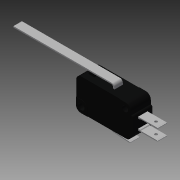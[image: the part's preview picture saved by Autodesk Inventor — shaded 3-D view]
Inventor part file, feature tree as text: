
AUTODESK INVENTOR PART (.ipt)
format: ipt  version: 2018 (Build 220112000, 112)  size: 339,968 bytes
history: native  units: in
note: dims shown in document units (in); Inventor stores cm internally (conversion verified against a paired STEP export)
features: extrude x6, sketch x2, hole x2
ambient origin geometry x8: Origin, YZ Plane, XZ Plane, XY Plane, X Axis, Y Axis, Z Axis, Center Point
bodies: Solid1 (feature_tree)
feature tree (10):
  sketch  "Sketch1"  dims[d0=0.8749in d1=0.8749in d2=1.135in d3=1.135in]
  extrude  "Extrusion1"  Depth=1.135in
  sketch  "Sketch2"  dims[d4=0.4054in d5=0.4054in d6=0.17in d7=0.0in d8=0.3854in d9=0.3854in d10=0.6024in d11=0.6024in d12=0.402in d13=0.402in d14=0.24in d15=0.24in d16=0.6529in d17=0.6529in d18=2.3471in d19=2.3471in d20=0.02in d21=0.02in d22=0.125in d23=0.125in d24=0.187in d25=0.187in d26=0.126in d27=0.126in d28=0.235in d29=0.235in d30=0.0104in d31=0.0104in d32=0.54in d33=0.54in d34=0.323in d35=0.323in d36=0.114in d37=0.114in d38=0.11in d39=0.11in d40=0.116in d41=0.116in d42=0.626in d43=0.626in d44=0.04in d45=0.04in d46=0.386in d47=0.0in d48=0.402in d49=0.0in d50=0.402in d51=0.0in d52=0.15in d53=0.0in d54=0.17in d55=0.0in d56=0.187in d57=0.0in d58=0.125in d59=0.0935in d60=0.055in d61=0.5in d62=0.375in d63=0.25in d64=0.5635in d65=0.75in d66=0.8108in d67=0.0935in d68=0.125in d69=0.055in d70=0.5in d71=0.375in d72=0.25in d73=0.5635in d74=0.75in d75=0.8108in]
  extrude  "Extrusion2"  Depth=0.17in TaperAngle=0.0deg
  extrude  "Extrusion3"  Depth=0.187in
  extrude  "Extrusion4"  Depth=0.187in
  extrude  "Extrusion5"  Depth=0.402in
  extrude  "Extrusion6"  Depth=0.24in
  hole  "Hole1"  [1 undecoded]
  hole  "Hole2"  [1 undecoded]
note: 2 required parameter values undecoded (feature->parameter linkage not recoverable at this tier; creation-order binding heuristic only, values carry confidence <= 0.55)
